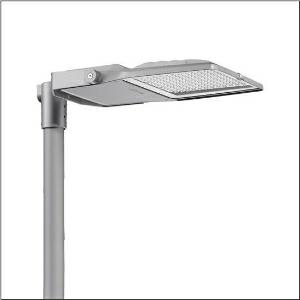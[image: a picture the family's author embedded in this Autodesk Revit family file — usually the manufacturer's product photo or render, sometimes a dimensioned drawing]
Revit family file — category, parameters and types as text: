
# Revit family: floodlight_fl_21_midi___pl64_5xa7781e2e3a_9b1f
name_source: partatom
category: Lighting Fixtures
units: mm (PartAtom-declared; Revit-internal decimal feet)

## family parameters
Cut with Voids When Loaded = No
Host = Face
Light Source = No
Part Type = Normal
Room Calculation Point = No
Round Connector Dimension = Use Diameter
Shared = No

## types (1)
- --- (1 x LED, 25930 lm, 208.1 W, 3000K)
    Apparent Load = 208 VA
    CIE Flux Codes = 28 80 98 100 100
    Color Rendering = 70
    Color Temperature = 3000K
    Default Elevation = 1800 mm
    Description = Floodlight FL 21 midi, floodlight, primary light control with lens, of PMMA, primary optical cover: protective disc, of toughened safety glass, transparent, light distribution: PL64, light emission: direct distribution, installation type: surface-mounted, LED, High Power LED, rated luminous flux: 25.930lm, luminous efficacy: 124lm/W, light colour: 730, colour temperature: 3000K, control gear: ECG iQ, control: optimised constant luminous flux control (CLO 2.0), Desk-Remote (wireless, voltage-free reading and setting of iQ features in the workshop via application-optimized NFC function/RFID function), Light-Fading, Smart-Wire, Night-Set, Lumen-Switch, Temp-Guard, Auto-Match, with terminal, 6-pole, mains connection: 220..240V, AC, 50/60Hz, start of lifetime: 208W, end of lifetime: 227W, reduction: 90W, luminaire housing, of diecast aluminium, powder-coated, Siteco® metallic grey (DB 702S), corrosivity category C5 according to DIN EN ISO 12944, mast bracket, of steel, galvanised, powder-coated, Siteco® metallic grey (DB 702S), protection rating (complete): IP66, insulation class (complete): insulation class I (protective earthing), certification: CE, protection symbol: D, impact resistance: IK08, permissible operating ambient temperature: -40..+40°C, permissible operating ambient temperature for outdoor applications: -40..+50°C, standard: DIN EN 12944, packaging unit: 1 piece

Light Distribution: PL64
    Height = 76 mm
    Lamp = 1 x LED
    Lamp Light Flux = 25930 lm
    Lamp Power = 208.1 W
    Lamp count = 1
    Length = 657 mm
    Luminous efficacy = 125 lm/W
    Manufacturer = Siteco
    ModVariant = No
    Model = 5XA7781E2E3A
    Number of Poles = 1
    OnlyDefault = Yes
    Power Factor = 1
    Product Name = Floodlight FL 21 midi | PL64
    Product group = floodlight | pylon top
    ProductGroupID = 6101
    Protection Class = Protection class I
    Protection Degree = IP 66
    RLX_Detail_Level = 1
    RlxData = <blob elided: 153545 chars, md5=93bc01ed>
    Socket = socket
    Standby Power = 0 W
    System Light Flux = 25930 lm
    System Power = 208 W
    Type Comments = factory setting: luminous flux: 100 % | dim-lin: 254 | 710 mA
    Type Image = l_1007123.jpg
    URL = http://relux.com
    VarID = @adj_015765
    Voltage = 0 V
    Weight = 0.00 kg
    Width = 442 mm

## geometry (parser evidence)
native form markers: Blend x4, Sweep x11
no freeform markers — native parametric forms only
